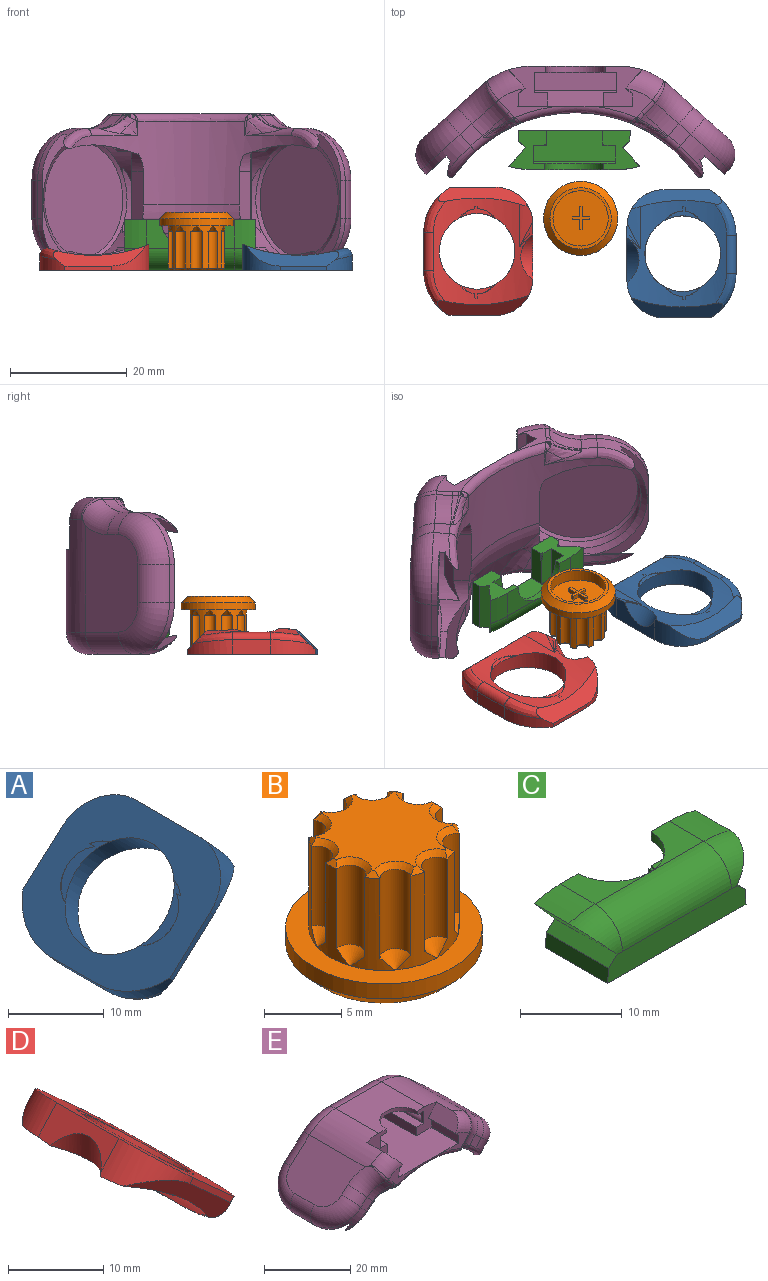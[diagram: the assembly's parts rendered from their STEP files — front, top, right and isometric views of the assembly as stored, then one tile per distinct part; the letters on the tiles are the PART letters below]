
ASSEMBLY  parts=5 mates=4
PART A: 36 faces, bbox 20x23.9x18.1 mm
  f0: cylinder r=25.31mm len=18.28mm, axis (0,1,0), area 126.4mm2, adj f2,f3,f4,f5,f6,f7,f8,f9
  f1: plane 21.95x13.89mm, normal (-0.67,0,0.74), area 225.5mm2, adj f10,f11,f13,f14,f17,f18,f19,f22
  f2: cylinder r=3.24mm len=1.7mm, axis (0.67,0,-0.74), area 0mm2, adj f0,f9,f34
  f3: cylinder r=3.24mm len=2.01mm, axis (0.67,0,-0.74), area 0.1mm2, adj f0,f8,f29,f34
  f4: cylinder r=3.24mm len=2.01mm, axis (0.67,0,-0.74), area 0.1mm2, adj f0,f6,f29,f32
  f5: cylinder r=3.24mm len=1.7mm, axis (0.67,0,-0.74), area 0mm2, adj f0,f7,f32
  f6: bspline ~4.55x2.83mm, area 0.3mm2, adj f0,f4,f29
  f7: bspline ~4.55x2.65mm, area 0.3mm2, adj f0,f5,f29
  f8: bspline ~4.55x2.83mm, area 0.3mm2, adj f0,f3,f29
  f9: bspline ~4.55x2.65mm, area 0.3mm2, adj f0,f2,f29
  f10: cone r=3.75mm half-angle=45deg, axis (-0.67,0,0.74), area 0.3mm2, adj f1,f29,f35
  f11: cone r=3.75mm half-angle=45deg, axis (-0.67,0,0.74), area 0.3mm2, adj f1,f29,f31
  f12: torus R=39.28mm, axis (0,1,0), area 0.4mm2, adj f0,f13,f25,f28
  f13: plane 9.51x3.46mm, normal (0.74,0,0.67), area 24.4mm2, adj f1,f12,f14,f25,f27,f28
  f14: cylinder r=6.35mm len=7.69mm, axis (-0.67,0,0.74), area 26.3mm2, adj f0,f1,f13,f23,f24,f28
  f15: cylinder r=1.27mm len=6.52mm, axis (0,1,0), area 15.5mm2, adj f0,f16,f18,f20
  f16: bspline ~9.5x4.45mm, area 15.4mm2, adj f0,f15,f17,f24
  f17: cylinder r=8.89mm len=7.63mm, axis (0.67,0,-0.74), area 18.3mm2, adj f1,f16,f18,f23,f24
  f18: plane 6.52x1.85mm, normal (-0.74,0,-0.67), area 16.2mm2, adj f1,f15,f17,f19
  f19: cylinder r=8.89mm len=7.8mm, axis (0.67,0,-0.74), area 18.8mm2, adj f1,f18,f20,f21,f22
  f20: bspline ~9.84x4.9mm, area 16.1mm2, adj f0,f15,f19,f21
  f21: plane 14.42x11.77mm, normal (0.47,0.71,-0.53), area 39.2mm2, adj f0,f19,f20,f22,f26,f27
  f22: plane 6.23x5.71mm, normal (0,1,0), area 5.6mm2, adj f1,f19,f21,f27
  f23: plane 6.45x5.91mm, normal (0,-1,0), area 5.8mm2, adj f1,f14,f17,f24
  f24: plane 14.65x11.84mm, normal (0.47,-0.71,-0.53), area 40mm2, adj f0,f14,f16,f17,f23
  f25: bspline ~4.3x3.46mm, area 3mm2, adj f12,f13,f26,f27
  f26: cylinder r=13.97mm len=7.21mm, axis (0,1,0), area 10.1mm2, adj f0,f21,f25,f27
  f27: cylinder r=6.35mm len=7.48mm, axis (0.67,0,-0.74), area 25.7mm2, adj f1,f13,f21,f22,f25,f26
  f28: cylinder r=4.57mm len=7.54mm, axis (0,0,-1), area 17.8mm2, adj f0,f12,f13,f14
  f29: cylinder r=6.48mm len=12.95mm, axis (0.68,0,-0.74), area 120.6mm2, adj f0,f1,f3,f4,f6,f7,f8,f9
  f30: cylinder r=4.51mm len=2.07mm, axis (0.68,0,-0.74), area 0mm2, adj f1,f29,f31
  f31: plane 5.8x5.31mm, normal (-0.68,0,0.74), area 7.7mm2, adj f1,f11,f29,f30
  f32: plane 3.94x3.61mm, normal (0.68,0,-0.74), area 3.5mm2, adj f0,f4,f5,f29
  f33: cylinder r=4.41mm len=1.85mm, axis (0.68,0,-0.74), area 0mm2, adj f1,f29,f35
  f34: plane 3.94x3.61mm, normal (0.68,0,-0.74), area 3.4mm2, adj f0,f2,f3,f29
  f35: plane 5.75x5.26mm, normal (-0.68,0,0.74), area 7.5mm2, adj f1,f10,f29,f33
PART B: 70 faces, bbox 12.7x12.7x9.9 mm
  f0: plane 9.47x9.47mm, normal (0,0,-1), area 67.3mm2, adj f24,f36,f37,f38,f39,f40,f41,f42
  f1: cylinder r=1.02mm len=6.27mm, axis (0,0,-1), area 18.7mm2, adj f2,f20,f33,f68
  f2: cylinder r=4.85mm len=7.24mm, axis (0,0,-1), area 8.3mm2, adj f1,f3,f22,f32,f33,f66
  f3: cylinder r=1.02mm len=6.27mm, axis (0,0,-1), area 18.7mm2, adj f2,f4,f32,f64
  f4: cylinder r=4.85mm len=7.24mm, axis (0,0,-1), area 8.3mm2, adj f3,f5,f22,f31,f32,f62
  f5: cylinder r=1.02mm len=6.27mm, axis (0,0,-1), area 18.7mm2, adj f4,f6,f31,f60
  f6: cylinder r=4.85mm len=7.24mm, axis (0,0,-1), area 8.3mm2, adj f5,f7,f22,f30,f31,f58
  f7: cylinder r=1.02mm len=6.27mm, axis (0,0,-1), area 18.7mm2, adj f6,f8,f30,f56
  f8: cylinder r=4.85mm len=7.24mm, axis (0,0,-1), area 8.3mm2, adj f7,f9,f22,f29,f30,f54
  f9: cylinder r=1.02mm len=6.27mm, axis (0,0,-1), area 18.7mm2, adj f8,f10,f29,f52
  f10: cylinder r=4.85mm len=7.24mm, axis (0,0,-1), area 8.3mm2, adj f9,f11,f22,f28,f29,f50
  f11: cylinder r=1.02mm len=6.27mm, axis (0,0,-1), area 18.7mm2, adj f10,f12,f28,f49
  f12: cylinder r=4.85mm len=7.24mm, axis (0,0,-1), area 8.3mm2, adj f11,f13,f22,f27,f28,f51
  f13: cylinder r=1.02mm len=6.27mm, axis (0,0,-1), area 18.7mm2, adj f12,f14,f27,f53
  f14: cylinder r=4.85mm len=7.24mm, axis (0,0,-1), area 8.3mm2, adj f13,f15,f22,f26,f27,f55
  f15: cylinder r=1.02mm len=6.27mm, axis (0,0,-1), area 18.7mm2, adj f14,f16,f26,f57
  f16: cylinder r=4.85mm len=7.24mm, axis (0,0,-1), area 8.3mm2, adj f15,f17,f22,f26,f35,f59
  f17: cylinder r=1.02mm len=6.27mm, axis (0,0,-1), area 18.7mm2, adj f16,f18,f35,f61
  f18: cylinder r=4.85mm len=7.24mm, axis (0,0,-1), area 8.3mm2, adj f17,f19,f22,f34,f35,f63
  f19: cylinder r=1.02mm len=6.27mm, axis (0,0,-1), area 18.7mm2, adj f18,f20,f34,f65
  f20: cylinder r=4.85mm len=7.24mm, axis (0,0,-1), area 8.3mm2, adj f1,f19,f22,f33,f34,f67
  f21: plane 8.94x8.57mm, normal (0,0,1), area 44.3mm2, adj f49,f50,f51,f52,f53,f54,f55,f56
  f22: plane 12.7x12.7mm, normal (0,0,1), area 52.8mm2, adj f2,f4,f6,f8,f10,f12,f14,f16
  f23: cylinder r=6.35mm len=12.7mm, axis (0,0,1), area 47.6mm2, adj f22,f69
  f24: cylinder r=4.74mm len=9.47mm, axis (0,0,1), area 60.5mm2, adj f0,f25
  f25: plane 10.52x10.52mm, normal (0,0,-1), area 16.3mm2, adj f24,f69
  f26: cone r=0.05mm half-angle=45deg, axis (0,0,1), area 2.2mm2, adj f14,f15,f16,f22
  f27: cone r=0.05mm half-angle=45deg, axis (0,0,1), area 2.2mm2, adj f12,f13,f14,f22
  f28: cone r=0.05mm half-angle=45deg, axis (0,0,1), area 2.2mm2, adj f10,f11,f12,f22
  f29: cone r=0.05mm half-angle=45deg, axis (0,0,1), area 2.2mm2, adj f8,f9,f10,f22
  f30: cone r=0.05mm half-angle=45deg, axis (0,0,1), area 2.2mm2, adj f6,f7,f8,f22
  f31: cone r=0.05mm half-angle=45deg, axis (0,0,1), area 2.2mm2, adj f4,f5,f6,f22
  f32: cone r=0.05mm half-angle=45deg, axis (0,0,1), area 2.2mm2, adj f2,f3,f4,f22
  f33: cone r=0.05mm half-angle=45deg, axis (0,0,1), area 2.2mm2, adj f1,f2,f20,f22
  f34: cone r=0.05mm half-angle=45deg, axis (0,0,1), area 2.2mm2, adj f18,f19,f20,f22
  f35: cone r=0.05mm half-angle=45deg, axis (0,0,1), area 2.2mm2, adj f16,f17,f18,f22
  f36: plane 0.76x0.51mm, normal (0,-1,0), area 0.4mm2, adj f0,f37,f47,f48
  f37: plane 1.73x0.76mm, normal (-1,0,0), area 1.3mm2, adj f0,f36,f38,f48
  f38: plane 1.21x0.76mm, normal (0,-1,0), area 0.9mm2, adj f0,f37,f39,f48
  f39: plane 0.76x0.51mm, normal (-1,0,0), area 0.4mm2, adj f0,f38,f40,f48
  f40: plane 1.21x0.76mm, normal (0,1,0), area 0.9mm2, adj f0,f39,f41,f48
  f41: plane 1.73x0.76mm, normal (-1,0,0), area 1.3mm2, adj f0,f40,f42,f48
  f42: plane 0.76x0.51mm, normal (0,1,0), area 0.4mm2, adj f0,f41,f43,f48
  f43: plane 1.73x0.76mm, normal (1,0,0), area 1.3mm2, adj f0,f42,f44,f48
  f44: plane 1.21x0.76mm, normal (0,1,0), area 0.9mm2, adj f0,f43,f45,f48
  f45: plane 0.76x0.51mm, normal (1,0,0), area 0.4mm2, adj f0,f44,f46,f48
  f46: plane 1.21x0.76mm, normal (0,-1,0), area 0.9mm2, adj f0,f45,f47,f48
  f47: plane 1.73x0.76mm, normal (1,0,0), area 1.3mm2, adj f0,f36,f46,f48
  f48: plane 3.96x2.92mm, normal (0,0,-1), area 3.2mm2, adj f36,f37,f38,f39,f40,f41,f42,f43
  f49: cone r=1.02mm half-angle=45deg, axis (0,0,1), area 1.7mm2, adj f11,f21,f50,f51
  f50: cone r=4.47mm half-angle=45deg, axis (0,0,-1), area 0.3mm2, adj f10,f21,f49,f52
  f51: cone r=4.47mm half-angle=45deg, axis (0,0,-1), area 0.3mm2, adj f12,f21,f49,f53
  f52: cone r=1.02mm half-angle=45deg, axis (0,0,1), area 1.7mm2, adj f9,f21,f50,f54
  f53: cone r=1.02mm half-angle=45deg, axis (0,0,1), area 1.7mm2, adj f13,f21,f51,f55
  f54: cone r=4.47mm half-angle=45deg, axis (0,0,-1), area 0.3mm2, adj f8,f21,f52,f56
  f55: cone r=4.47mm half-angle=45deg, axis (0,0,-1), area 0.3mm2, adj f14,f21,f53,f57
  f56: cone r=1.02mm half-angle=45deg, axis (0,0,1), area 1.7mm2, adj f7,f21,f54,f58
  f57: cone r=1.02mm half-angle=45deg, axis (0,0,1), area 1.7mm2, adj f15,f21,f55,f59
  f58: cone r=4.47mm half-angle=45deg, axis (0,0,-1), area 0.3mm2, adj f6,f21,f56,f60
  f59: cone r=4.47mm half-angle=45deg, axis (0,0,-1), area 0.3mm2, adj f16,f21,f57,f61
  f60: cone r=1.02mm half-angle=45deg, axis (0,0,1), area 1.7mm2, adj f5,f21,f58,f62
  f61: cone r=1.02mm half-angle=45deg, axis (0,0,1), area 1.7mm2, adj f17,f21,f59,f63
  f62: cone r=4.47mm half-angle=45deg, axis (0,0,-1), area 0.3mm2, adj f4,f21,f60,f64
  f63: cone r=4.47mm half-angle=45deg, axis (0,0,-1), area 0.3mm2, adj f18,f21,f61,f65
  f64: cone r=1.02mm half-angle=45deg, axis (0,0,1), area 1.7mm2, adj f3,f21,f62,f66
  f65: cone r=1.02mm half-angle=45deg, axis (0,0,1), area 1.7mm2, adj f19,f21,f63,f67
  f66: cone r=4.47mm half-angle=45deg, axis (0,0,-1), area 0.3mm2, adj f2,f21,f64,f68
  f67: cone r=4.47mm half-angle=45deg, axis (0,0,-1), area 0.3mm2, adj f20,f21,f65,f68
  f68: cone r=1.02mm half-angle=45deg, axis (0,0,1), area 1.7mm2, adj f1,f21,f66,f67
  f69: cone r=5.26mm half-angle=45deg, axis (0,0,1), area 56.3mm2, adj f23,f25
PART C: 31 faces, bbox 22.5x8.6x6.9 mm
  f0: plane 6.71x6.45mm, normal (0,1,0), area 24.9mm2, adj f2,f3,f9,f10,f14,f16,f17,f18
  f1: plane 7.55x4.83mm, normal (0,0,1), area 17.5mm2, adj f4,f5,f13,f26
  f2: plane 7.55x4.83mm, normal (0,0,1), area 17.5mm2, adj f0,f5,f14,f26
  f3: plane 19.21x8.64mm, normal (0,0,-1), area 105.4mm2, adj f0,f4,f7,f15,f16,f19,f20,f24
  f4: plane 6.65x6.45mm, normal (0,1,0), area 24.7mm2, adj f1,f3,f11,f12,f13,f15,f20,f21
  f5: cylinder r=3.81mm len=15.11mm, axis (1,0,0), area 90.4mm2, adj f1,f2,f6,f7,f8
  f6: torus R=8.89mm, axis (0,-1,0), area 15.8mm2, adj f5,f7,f9,f10,f14
  f7: plane 19.21x2.9mm, normal (0,-1,0), area 53.4mm2, adj f3,f5,f6,f8,f9,f12,f15,f16
  f8: torus R=8.89mm, axis (0,-1,0), area 15.8mm2, adj f5,f7,f11,f12,f13
  f9: plane 8.64x1.21mm, normal (0.67,0,0.74), area 14.1mm2, adj f0,f6,f7,f10,f16
  f10: plane 8.64x3.23mm, normal (0.74,0,-0.67), area 34mm2, adj f0,f6,f9,f14
  f11: plane 8.64x3.23mm, normal (-0.74,0,-0.67), area 34mm2, adj f4,f8,f12,f13
  f12: plane 8.64x1.21mm, normal (-0.67,0,0.74), area 14.1mm2, adj f4,f7,f8,f11,f15
  f13: cylinder r=12.7mm len=4.83mm, axis (0,1,0), area 17.9mm2, adj f1,f4,f8,f11
  f14: cylinder r=12.7mm len=4.83mm, axis (0,1,0), area 17.9mm2, adj f0,f2,f6,f10
  f15: plane 8.64x1.78mm, normal (-1,0,0.05), area 15.4mm2, adj f3,f4,f7,f12
  f16: plane 8.64x1.85mm, normal (1,0,0.05), area 16mm2, adj f0,f3,f7,f9
  f17: plane 6.35x3.05mm, normal (-1,0,0), area 19.3mm2, adj f0,f18,f23,f24,f25
  f18: plane 6.35x2.29mm, normal (0,0,1), area 14.2mm2, adj f0,f17,f19,f24,f30
  f19: plane 6.35x2.57mm, normal (-1,0,0), area 16mm2, adj f0,f3,f18,f24,f29,f30
  f20: plane 6.35x2.54mm, normal (1,0,0), area 15.8mm2, adj f3,f4,f21,f24,f27,f28
  f21: plane 6.35x2.29mm, normal (0,0,1), area 14.2mm2, adj f4,f20,f22,f24,f27
  f22: plane 6.35x3.05mm, normal (1,0,0), area 19.3mm2, adj f4,f21,f23,f24,f25
  f23: plane 14.1x5.97mm, normal (0,0,-1), area 46.2mm2, adj f0,f4,f17,f22,f25,f26
  f24: plane 14.1x5.24mm, normal (0,1,0), area 62mm2, adj f3,f17,f18,f19,f20,f21,f22,f25
  f25: plane 14.1x0.38mm, normal (0,0.71,-0.71), area 7.6mm2, adj f17,f22,f23,f24
  f26: cylinder r=5.08mm len=10.15mm, axis (0,0,1), area 16.5mm2, adj f0,f1,f2,f4,f23
  f27: cylinder r=5.08mm len=1.51mm, axis (0,0,1), area 0.4mm2, adj f4,f20,f21,f28
  f28: plane 1.51x0.31mm, normal (0,0,1), area 0.3mm2, adj f4,f20,f27
  f29: plane 1.51x0.31mm, normal (0,0,1), area 0.3mm2, adj f0,f19,f30
  f30: cylinder r=5.08mm len=1.51mm, axis (0,0,1), area 0.4mm2, adj f0,f18,f19,f29
PART D: 37 faces, bbox 20x23.9x18.1 mm
  f0: cylinder r=3.24mm len=1.7mm, axis (-0.67,0,-0.74), area 0mm2, adj f5,f7,f36
  f1: cone r=3.75mm half-angle=45deg, axis (0.67,0,0.74), area 0.3mm2, adj f22,f29,f35
  f2: cylinder r=3.24mm len=2.01mm, axis (-0.67,0,-0.74), area 0.1mm2, adj f5,f10,f29,f33
  f3: cone r=3.75mm half-angle=45deg, axis (0.67,0,0.74), area 0.8mm2, adj f22,f29,f30,f32
  f4: torus R=39.28mm, axis (0,1,0), area 0.4mm2, adj f5,f19,f26,f28
  f5: cylinder r=25.31mm len=18.28mm, axis (0,1,0), area 126.6mm2, adj f0,f2,f4,f6,f7,f8,f9,f10
  f6: cylinder r=6.35mm len=7.69mm, axis (-0.67,0,-0.74), area 26.3mm2, adj f5,f22,f23,f24,f26,f28
  f7: bspline ~4.55x2.65mm, area 0.3mm2, adj f0,f5,f29
  f8: bspline ~4.55x2.83mm, area 0.3mm2, adj f5,f15,f29
  f9: bspline ~4.55x2.65mm, area 0.3mm2, adj f5,f16,f29
  f10: bspline ~4.55x2.83mm, area 0.3mm2, adj f2,f5,f29
  f11: cylinder r=1.27mm len=6.52mm, axis (0,1,0), area 15.5mm2, adj f5,f12,f13,f17
  f12: bspline ~9.03x3.93mm, area 15.4mm2, adj f5,f11,f14,f24
  f13: plane 6.52x1.85mm, normal (0.74,0,-0.67), area 16.2mm2, adj f11,f14,f18,f22
  f14: cylinder r=8.89mm len=7.63mm, axis (0.67,0,0.74), area 18.3mm2, adj f12,f13,f22,f23,f24
  f15: cylinder r=3.24mm len=2.01mm, axis (-0.67,0,-0.74), area 0.1mm2, adj f5,f8,f29,f36
  f16: cylinder r=3.24mm len=1.7mm, axis (-0.67,0,-0.74), area 0mm2, adj f5,f9,f33
  f17: bspline ~9.5x4.45mm, area 16.1mm2, adj f5,f11,f18,f20
  f18: cylinder r=8.89mm len=7.8mm, axis (0.67,0,0.74), area 18.8mm2, adj f13,f17,f20,f21,f22
  f19: bspline ~4.3x3.46mm, area 3mm2, adj f4,f25,f26,f27
  f20: plane 14.42x11.78mm, normal (-0.47,0.71,-0.53), area 39.1mm2, adj f5,f17,f18,f21,f25,f27
  f21: plane 6.23x5.71mm, normal (0,1,0), area 5.6mm2, adj f18,f20,f22,f27
  f22: plane 21.95x13.9mm, normal (0.67,0,0.74), area 225.9mm2, adj f1,f3,f6,f13,f14,f18,f21,f23
  f23: plane 6.45x5.91mm, normal (0,-1,0), area 5.8mm2, adj f6,f14,f22,f24
  f24: plane 14.65x11.84mm, normal (-0.47,-0.71,-0.53), area 40mm2, adj f5,f6,f12,f14,f23
  f25: cylinder r=13.97mm len=7.21mm, axis (0,1,0), area 10.1mm2, adj f5,f19,f20,f27
  f26: plane 9.51x3.46mm, normal (-0.74,0,0.67), area 24.4mm2, adj f4,f6,f19,f22,f27,f28
  f27: cylinder r=6.35mm len=7.48mm, axis (0.67,0,0.74), area 25.7mm2, adj f19,f20,f21,f22,f25,f26
  f28: cylinder r=4.57mm len=7.54mm, axis (0,0,-1), area 17.8mm2, adj f4,f5,f6,f26
  f29: cylinder r=6.48mm len=12.95mm, axis (-0.68,0,-0.74), area 120.4mm2, adj f1,f2,f3,f5,f7,f8,f9,f10
  f30: plane 5.37x4.91mm, normal (0.68,0,0.74), area 6.7mm2, adj f3,f22,f29,f31,f32
  f31: cylinder r=4.07mm len=1.12mm, axis (-0.68,0,-0.74), area 0mm2, adj f22,f29,f30
  f32: cylinder r=4.07mm len=3.48mm, axis (-0.68,0,-0.74), area 0mm2, adj f3,f30
  f33: plane 3.94x3.61mm, normal (-0.68,0,-0.74), area 3.3mm2, adj f2,f5,f16,f29
  f34: cylinder r=4.48mm len=2.21mm, axis (-0.68,0,-0.74), area 0mm2, adj f22,f29,f35
  f35: plane 5.85x5.36mm, normal (0.68,0,0.74), area 7.8mm2, adj f1,f22,f29,f34
  f36: plane 3.94x3.61mm, normal (-0.68,0,-0.74), area 3.5mm2, adj f0,f5,f15,f29
PART E: 164 faces, bbox 57.7x34x23.8 mm
  f0: cylinder r=10.41mm len=20.83mm, axis (0.67,0,-0.74), area 140.7mm2, adj f70,f71,f73,f74,f116,f122,f149,f150
  f1: plane 15.75x3.43mm, normal (1,0,0), area 24.3mm2, adj f5,f111,f112,f123,f124,f148,f150,f162
  f2: plane 15.75x3.43mm, normal (-1,0,0), area 24.3mm2, adj f3,f111,f115,f123,f124,f153,f155,f163
  f3: plane 6.94x6.69mm, normal (0,-1,0), area 27mm2, adj f2,f4,f6,f106,f107,f108,f109,f110
  f4: plane 15.11x14.14mm, normal (0,0,1), area 173.1mm2, adj f3,f5,f6,f7,f91,f125
  f5: plane 6.88x6.69mm, normal (0,-1,0), area 26.8mm2, adj f1,f4,f7,f103,f104,f105,f106,f111
  f6: cylinder r=12.7mm len=19.22mm, axis (0,1,0), area 158.4mm2, adj f3,f4,f43,f93,f100,f110,f137
  f7: cylinder r=12.7mm len=19.22mm, axis (0,1,0), area 158.4mm2, adj f4,f5,f11,f42,f89,f103,f126
  f8: plane 9.84x4.88mm, normal (0,-1,0), area 14.3mm2, adj f10,f11,f104,f105,f106,f129,f130,f131
  f9: plane 9.64x4.88mm, normal (0,-1,0), area 14mm2, adj f10,f100,f106,f107,f108,f109,f140,f141
  f10: torus R=26.58mm, axis (0,-1,0), area 38.5mm2, adj f8,f9,f12,f106,f134,f135,f136,f145
  f11: torus R=8.89mm, axis (0,-1,0), area 27.7mm2, adj f7,f8,f103,f104,f127,f128
  f12: cylinder r=25.31mm len=40.92mm, axis (0,1,0), area 321.2mm2, adj f10,f14,f20,f25,f37,f39,f60,f61
  f13: cylinder r=13.97mm len=5.07mm, axis (0,1,0), area 14.8mm2, adj f16,f26,f31,f46,f53,f74
  f14: torus R=39.28mm, axis (0,1,0), area 76.6mm2, adj f12,f16,f17,f44,f64,f65
  f15: cylinder r=13.97mm len=5.07mm, axis (0,1,0), area 14.8mm2, adj f17,f21,f30,f48,f58,f76
  f16: bspline ~6.48x5.29mm, area 7.5mm2, adj f13,f14,f46,f65,f74
  f17: bspline ~8.33x6.71mm, area 7.5mm2, adj f14,f15,f48,f64,f76
  f18: plane 22.35x6.9mm, normal (-0.67,0,-0.74), area 34.8mm2, adj f19,f22,f28,f33,f35,f117
  f19: plane 6.96x6.56mm, normal (0,1,0), area 8.6mm2, adj f18,f20,f35,f75,f117
  f20: plane 15.09x12.05mm, normal (0.47,0.71,0.53), area 38.8mm2, adj f12,f19,f35,f39,f75
  f21: plane 14.06x11.28mm, normal (0.47,-0.71,0.53), area 37.8mm2, adj f15,f22,f30,f33,f38,f76
  f22: plane 6.71x6.34mm, normal (0,-1,0), area 8.3mm2, adj f18,f21,f33,f76,f117
  f23: plane 22.35x6.9mm, normal (0.67,0,-0.74), area 34.8mm2, adj f24,f27,f29,f32,f34,f116
  f24: plane 6.96x6.56mm, normal (0,1,0), area 8.6mm2, adj f23,f25,f34,f73,f116
  f25: plane 15.09x12.05mm, normal (-0.47,0.71,0.53), area 38.8mm2, adj f12,f24,f34,f37,f73
  f26: plane 14.06x11.28mm, normal (-0.47,-0.71,0.53), area 37.8mm2, adj f13,f27,f31,f32,f36,f74
  f27: plane 6.71x6.34mm, normal (0,-1,0), area 8.3mm2, adj f23,f26,f32,f74,f116
  f28: plane 6.52x0.85mm, normal (0.74,0,-0.67), area 7.5mm2, adj f18,f33,f35,f98
  f29: plane 6.52x0.85mm, normal (-0.74,0,-0.67), area 7.5mm2, adj f23,f32,f34,f90
  f30: cylinder r=25.31mm len=9.51mm, axis (0,1,0), area 22.3mm2, adj f15,f21,f38,f59
  f31: cylinder r=25.31mm len=9.51mm, axis (0,1,0), area 22.3mm2, adj f13,f26,f36,f55
  f32: cylinder r=8.89mm len=8.89mm, axis (0.67,0,-0.74), area 23.3mm2, adj f23,f26,f27,f29,f36,f50,f88
  f33: cylinder r=8.89mm len=8.89mm, axis (0.67,0,0.74), area 23.3mm2, adj f18,f21,f22,f28,f38,f50,f97
  f34: cylinder r=8.89mm len=8.89mm, axis (0.67,0,-0.74), area 24.1mm2, adj f23,f24,f25,f29,f37,f41,f92
  f35: cylinder r=8.89mm len=8.89mm, axis (0.67,0,0.74), area 24.1mm2, adj f18,f19,f20,f28,f39,f40,f99
  f36: bspline ~7.85x7.18mm, area 13.1mm2, adj f26,f31,f32,f55
  f37: bspline ~8.21x7.4mm, area 13.8mm2, adj f12,f25,f34,f60
  f38: bspline ~7.41x6.89mm, area 13.1mm2, adj f21,f30,f33,f59
  f39: bspline ~7.85x7.18mm, area 13.8mm2, adj f12,f20,f35,f63
  f40: plane 3.86x3.78mm, normal (0,-1,0), area 7.3mm2, adj f35,f63,f77,f101
  f41: plane 3.86x3.78mm, normal (0,-1,0), area 7.3mm2, adj f34,f60,f82,f94
  f42: plane 18.19x10.02mm, normal (-0.67,0,0.74), area 216.5mm2, adj f7,f87,f88,f90,f92,f94,f96
  f43: plane 18.19x10.02mm, normal (0.67,0,0.74), area 216.5mm2, adj f6,f95,f97,f98,f99,f101,f102
  f44: cone r=29.12mm half-angle=20.6deg, axis (0,1,0), area 46.9mm2, adj f14,f45,f46,f48
  f45: torus R=15.15mm, axis (0,-1,0), area 0.3mm2, adj f44,f47,f49,f54
  f46: bspline ~10.91x6.7mm, area 18.8mm2, adj f13,f16,f44,f47,f51
  f47: bspline ~5.27x4.34mm, area 0mm2, adj f45,f46,f52
  f48: bspline ~9.02x6.04mm, area 18.8mm2, adj f15,f17,f44,f49,f57
  f49: bspline ~4.48x4.13mm, area 0mm2, adj f45,f48,f56
  f50: plane 39.49x9.87mm, normal (0,1,0), area 99.5mm2, adj f32,f33,f51,f52,f53,f54,f55,f56
  f51: bspline ~6.72x4.14mm, area 8.6mm2, adj f46,f50,f52,f53
  f52: bspline ~1.28x0.87mm, area 0.3mm2, adj f47,f50,f51,f54
  f53: torus R=12.7mm, axis (0,-1,0), area 10.1mm2, adj f13,f50,f51,f55
  f54: torus R=29.45mm, axis (0,-1,0), area 7.9mm2, adj f45,f50,f52,f56
  f55: torus R=26.58mm, axis (0,-1,0), area 15.5mm2, adj f31,f36,f50,f53
  f56: bspline ~1.25x0.84mm, area 0.3mm2, adj f49,f50,f54,f57
  f57: bspline ~6.78x4.19mm, area 8.6mm2, adj f48,f50,f56,f58
  f58: torus R=12.7mm, axis (0,-1,0), area 10.1mm2, adj f15,f50,f57,f59
  f59: torus R=26.58mm, axis (0,-1,0), area 15.5mm2, adj f30,f38,f50,f58
  f60: torus R=26.58mm, axis (0,1,0), area 8.8mm2, adj f12,f37,f41,f83,f84,f85,f86
  f61: cylinder r=1.27mm len=2.6mm, axis (0,1,0), area 0.4mm2, adj f12,f85,f135
  f62: cylinder r=1.27mm len=2.6mm, axis (0,1,0), area 0.4mm2, adj f12,f80,f147
  f63: torus R=26.58mm, axis (0,1,0), area 8.8mm2, adj f12,f39,f40,f78,f79,f80,f81
  f64: plane 9.88x2.32mm, normal (0.74,0,-0.67), area 26.5mm2, adj f12,f14,f17,f75,f76,f119
  f65: plane 9.88x2.46mm, normal (-0.74,0,-0.67), area 28.4mm2, adj f12,f14,f16,f71,f73,f74
  f66: plane 19.9x14.81mm, normal (-0.67,0,-0.74), area 308.2mm2, adj f121,f160,f161
  f67: plane 9.97x0.94mm, normal (0.67,0,0.74), area 8.5mm2, adj f68,f72
  f68: cylinder r=10.41mm len=20.83mm, axis (-0.67,0,-0.74), area 140.9mm2, adj f67,f72,f75,f76,f117,f118,f120,f121
  f69: plane 19.9x14.81mm, normal (0.67,0,-0.74), area 308.2mm2, adj f122,f158,f159
  f70: plane 9.97x0.94mm, normal (-0.67,0,0.74), area 8.5mm2, adj f0,f71
  f71: plane 16.96x4.4mm, normal (-1,0,0.05), area 33.5mm2, adj f0,f65,f70,f73,f74
  f72: plane 15.86x3.38mm, normal (1,0,0.05), area 30.3mm2, adj f67,f68,f118,f119,f120
  f73: cylinder r=6.35mm len=8.43mm, axis (0.67,0,-0.74), area 24.1mm2, adj f0,f12,f24,f25,f65,f71,f116
  f74: cylinder r=6.35mm len=8.17mm, axis (-0.67,0,0.74), area 23.2mm2, adj f0,f13,f16,f26,f27,f65,f71,f116
  f75: cylinder r=6.35mm len=8.43mm, axis (-0.67,0,-0.74), area 23.3mm2, adj f12,f19,f20,f64,f68,f117,f118
  f76: cylinder r=6.35mm len=8.17mm, axis (0.67,0,0.74), area 22.3mm2, adj f15,f17,f21,f22,f64,f68,f117,f120
  f77: cylinder r=7.62mm len=5.86mm, axis (-0.67,0,-0.74), area 16.5mm2, adj f40,f78,f102,f139,f140
  f78: bspline ~5.88x4.79mm, area 3.6mm2, adj f63,f77,f79,f141
  f79: bspline ~5.37x3.39mm, area 1.5mm2, adj f63,f78,f81,f142
  f80: bspline ~4.93x4.83mm, area 4.7mm2, adj f62,f63,f81,f146
  f81: bspline ~6.23x3.41mm, area 7.9mm2, adj f63,f79,f80,f143,f144,f145
  f82: cylinder r=7.62mm len=5.86mm, axis (0.67,0,-0.74), area 16.5mm2, adj f41,f83,f96,f128,f129
  f83: bspline ~5.39x4.52mm, area 3.6mm2, adj f60,f82,f84,f130
  f84: bspline ~5.35x3.43mm, area 1.5mm2, adj f60,f83,f86,f131
  f85: bspline ~4.93x4.83mm, area 4.7mm2, adj f60,f61,f86,f136
  f86: bspline ~6.25x3.43mm, area 7.9mm2, adj f60,f84,f85,f132,f133,f134
  f87: cylinder r=3.81mm len=8.79mm, axis (-0.74,0,-0.67), area 50.3mm2, adj f42,f50,f88,f89
  f88: torus R=5.08mm, axis (0.67,0,-0.74), area 70.6mm2, adj f32,f42,f87,f90
  f89: torus R=8.89mm, axis (0,-1,0), area 49.6mm2, adj f7,f50,f87,f91
  f90: cylinder r=3.81mm len=6.52mm, axis (0,1,0), area 39mm2, adj f29,f42,f88,f92
  f91: cylinder r=3.81mm len=15.11mm, axis (1,0,0), area 90.4mm2, adj f4,f50,f89,f93
  f92: torus R=5.08mm, axis (0.67,0,-0.74), area 70.6mm2, adj f34,f42,f90,f94
  f93: torus R=8.89mm, axis (0,-1,0), area 49.6mm2, adj f6,f50,f91,f95
  f94: cylinder r=3.81mm len=4.65mm, axis (-0.74,0,-0.67), area 16.3mm2, adj f41,f42,f92,f96
  f95: cylinder r=3.81mm len=8.79mm, axis (-0.74,0,0.67), area 50.3mm2, adj f43,f50,f93,f97
  f96: torus R=11.43mm, axis (0.67,0,-0.74), area 37.2mm2, adj f42,f82,f94,f126,f127
  f97: torus R=5.08mm, axis (-0.67,0,-0.74), area 70.6mm2, adj f33,f43,f95,f98
  f98: cylinder r=3.81mm len=6.52mm, axis (0,-1,0), area 39mm2, adj f28,f43,f97,f99
  f99: torus R=5.08mm, axis (-0.67,0,-0.74), area 70.6mm2, adj f35,f43,f98,f101
  f100: torus R=8.89mm, axis (0,-1,0), area 27.7mm2, adj f6,f9,f109,f110,f138,f139
  f101: cylinder r=3.81mm len=4.65mm, axis (-0.74,0,0.67), area 16.3mm2, adj f40,f43,f99,f102
  f102: torus R=11.43mm, axis (-0.67,0,-0.74), area 37.2mm2, adj f43,f77,f101,f137,f138
  f103: plane 8.89x3.14mm, normal (0.74,0,0.67), area 34.1mm2, adj f5,f7,f11,f104
  f104: plane 8.89x1.11mm, normal (0.67,0,-0.74), area 13.3mm2, adj f5,f8,f11,f103,f105
  f105: plane 8.89x2.11mm, normal (1,0,-0.05), area 18.8mm2, adj f5,f8,f104,f106
  f106: plane 20.03x19.46mm, normal (0,0,1), area 278.7mm2, adj f3,f5,f8,f9,f10,f105,f107,f113
  f107: plane 8.89x0.23mm, normal (0,0,1), area 2mm2, adj f3,f9,f106,f108
  f108: plane 8.89x2.19mm, normal (-1,0,-0.05), area 19.5mm2, adj f3,f9,f107,f109
  f109: plane 8.89x1.11mm, normal (-0.67,0,-0.74), area 13.3mm2, adj f3,f9,f100,f108,f110
  f110: plane 8.89x3.14mm, normal (-0.74,0,0.67), area 34.1mm2, adj f3,f6,f100,f109
  f111: plane 15.75x14.1mm, normal (0,0,-1), area 181.5mm2, adj f1,f2,f3,f5,f123,f125
  f112: plane 15.11x2.29mm, normal (0,0,1), area 34.6mm2, adj f1,f5,f113,f124
  f113: plane 15.11x2.39mm, normal (1,0,0), area 31.3mm2, adj f5,f106,f112,f124
  f114: plane 15.11x2.42mm, normal (-1,0,0), area 31.7mm2, adj f3,f106,f115,f124
  f115: plane 15.11x2.29mm, normal (0,0,1), area 34.6mm2, adj f2,f3,f114,f124
  f116: cone r=11.43mm half-angle=53.1deg, axis (0.67,0,-0.74), area 51.3mm2, adj f0,f23,f24,f27,f73,f74
  f117: cone r=11.43mm half-angle=53.1deg, axis (-0.67,0,-0.74), area 51.3mm2, adj f18,f19,f22,f68,f75,f76
  f118: bspline ~3.66x1.79mm, area 1.4mm2, adj f68,f72,f75,f119
  f119: cylinder r=0.46mm len=9.65mm, axis (0,1,0), area 3.5mm2, adj f64,f72,f118,f120
  f120: bspline ~3.66x1.79mm, area 1.4mm2, adj f68,f72,f76,f119
  f121: cone r=10.41mm half-angle=45deg, axis (-0.67,0,-0.74), area 45.9mm2, adj f66,f68,f153
  f122: cone r=10.41mm half-angle=45deg, axis (0.67,0,-0.74), area 45.9mm2, adj f0,f69,f148
  f123: plane 14.1x3.05mm, normal (0,-1,0), area 43mm2, adj f1,f2,f111,f124
  f124: plane 14.1x4.67mm, normal (0,-0.51,0.86), area 55mm2, adj f1,f2,f106,f112,f113,f114,f115,f123
  f125: cylinder r=5.08mm len=10.16mm, axis (0,0,1), area 17mm2, adj f3,f4,f5,f111
  f126: bspline ~1.74x1.04mm, area 0.1mm2, adj f7,f96,f127
  f127: bspline ~4.04x3.97mm, area 3.3mm2, adj f11,f96,f126,f128
  f128: bspline ~1.32x1.28mm, area 0mm2, adj f11,f82,f127,f129
  f129: cylinder r=1.02mm len=2.52mm, axis (0.67,0,-0.74), area 2.2mm2, adj f8,f82,f128,f130
  f130: bspline ~1.65x1.59mm, area 0.9mm2, adj f8,f83,f129,f131
  f131: bspline ~0.94x0.85mm, area 0.2mm2, adj f8,f84,f130,f132
  f132: bspline ~0.87x0.53mm, area 0.1mm2, adj f86,f131,f133
  f133: bspline ~0.99x0.71mm, area 0.3mm2, adj f8,f86,f132,f134
  f134: bspline ~1.25x1.17mm, area 0.9mm2, adj f10,f86,f133,f136
  f135: bspline ~0.61x0.6mm, area 0mm2, adj f10,f61,f136
  f136: bspline ~0.85x0.51mm, area 0.2mm2, adj f10,f85,f134,f135
  f137: bspline ~3.54x1.99mm, area 0.1mm2, adj f6,f102,f138
  f138: bspline ~4.04x3.97mm, area 3.3mm2, adj f100,f102,f137,f139
  f139: bspline ~1.32x1.28mm, area 0mm2, adj f77,f100,f138,f140
  f140: cylinder r=1.02mm len=2.52mm, axis (-0.67,0,-0.74), area 2.2mm2, adj f9,f77,f139,f141
  f141: bspline ~2.3x2.18mm, area 0.9mm2, adj f9,f78,f140,f142
  f142: bspline ~0.94x0.85mm, area 0.2mm2, adj f9,f79,f141,f143
  f143: bspline ~0.87x0.53mm, area 0.1mm2, adj f81,f142,f144
  f144: bspline ~1x0.74mm, area 0.2mm2, adj f9,f81,f143,f145
  f145: bspline ~1.25x1.19mm, area 0.9mm2, adj f10,f81,f144,f146
  f146: bspline ~0.91x0.55mm, area 0.2mm2, adj f10,f80,f145,f147
  f147: bspline ~0.61x0.6mm, area 0mm2, adj f10,f62,f146
  f148: extruded ~13.72x4.79mm, area 54.2mm2, adj f1,f122,f149,f150,f151,f152,f162
  f149: plane 11.88x3.52mm, normal (0,0,1), area 25.3mm2, adj f0,f148,f150,f152,f162
  f150: plane 4.79x1.79mm, normal (0,1,0), area 2.8mm2, adj f0,f1,f148,f149,f151,f162
  f151: plane 0.77x0.64mm, normal (1,0,0), area 0.1mm2, adj f0,f148,f150
  f152: plane 1.9x0.83mm, normal (1,0,0), area 0.4mm2, adj f0,f148,f149
  f153: extruded ~13.72x4.79mm, area 54.2mm2, adj f2,f121,f154,f155,f156,f157,f163
  f154: plane 11.89x3.53mm, normal (0,0,1), area 25.3mm2, adj f68,f153,f155,f157,f163
  f155: plane 4.79x1.79mm, normal (0,1,0), area 2.8mm2, adj f2,f68,f153,f154,f156,f163
  f156: plane 0.77x0.64mm, normal (-1,0,0), area 0.1mm2, adj f68,f153,f155
  f157: plane 1.9x0.83mm, normal (-1,0,0), area 0.4mm2, adj f68,f153,f154
  f158: plane 2.25x0.04mm, normal (1,0,0), area 0.1mm2, adj f69,f159
  f159: extruded ~2.25x0.04mm, area 0mm2, adj f69,f158
  f160: plane 2.25x0.04mm, normal (-1,0,0), area 0.1mm2, adj f66,f161
  f161: extruded ~2.25x0.04mm, area 0mm2, adj f66,f160
  f162: cylinder r=1.27mm len=13.72mm, axis (0,-1,0), area 25.5mm2, adj f1,f148,f149,f150
  f163: cylinder r=1.27mm len=13.72mm, axis (0,1,0), area 25.5mm2, adj f2,f153,f154,f155
PLACE A rot(axis=(0,-1,0),138deg) t=(30.65,-12.52,13.29)mm
PLACE B rot(axis=(1,0,0),180deg) t=(13.16,8.18,-6.97)mm
PLACE C rot(axis=(1,0,0),90deg) t=(12.06,49.81,-14.46)mm
PLACE D rot(axis=(0,1,0),138deg) t=(-4.58,-12.1,13.29)mm
PLACE E rot(axis=(-1,0,0),90deg) t=(12.26,0.97,12.13)mm fixed
MATE planar A.f1 <-> C.f7  axis (0,0,-1) through (30.22,2.1,-14.59)mm
MATE planar B.f8 <-> A.f1  axis (0,0,-1) through (13.16,8.18,-14.59)mm
MATE planar D.f22 <-> E.f50  axis (0,0,-1) through (-4.14,2.54,-14.59)mm
MATE planar D.f22 <-> A.f1  axis (0,0,-1) through (-4.14,2.54,-14.59)mm
